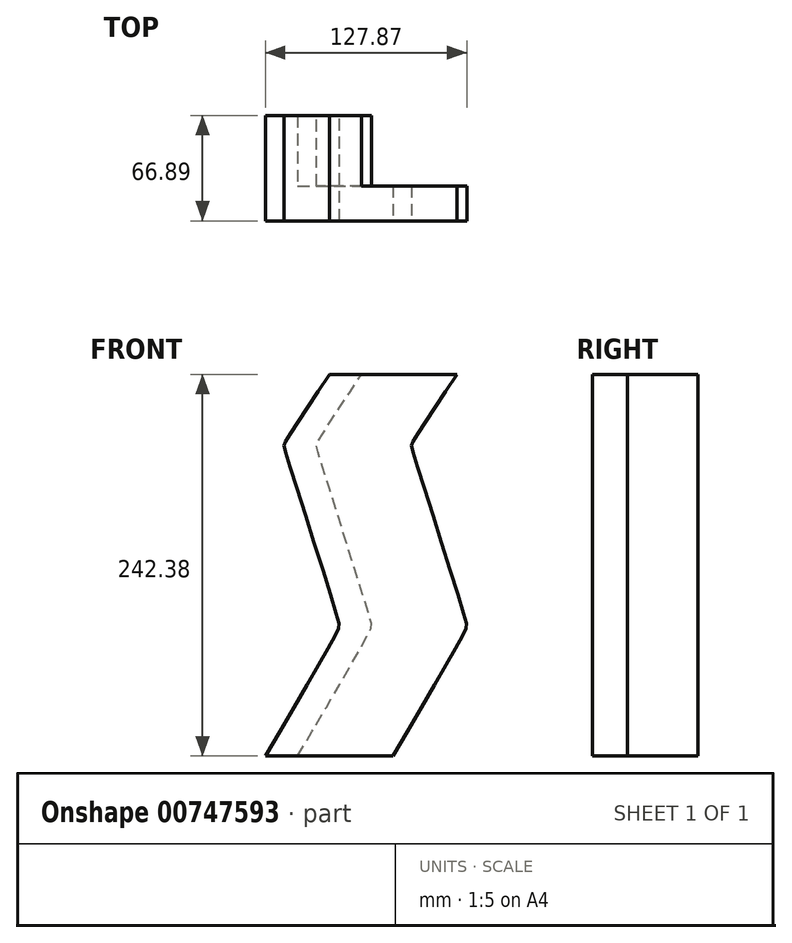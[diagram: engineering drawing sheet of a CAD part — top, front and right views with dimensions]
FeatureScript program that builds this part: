
annotation { "Feature Type Name" : "Feature", "Feature Type Description" : "" }
export const myFeature = defineFeature(function(context is Context, id is Id, definition is map)
    precondition{}
    {
        {
            var Q0;
            Q0=qCreatedBy(makeId("Top.planeOp"),FACE);
            var sketch = newSketch(context, id + "F0", { "sketchPlane" : qUnion([Q0])});
            skLineSegment(sketch, "E0.bottom", {"start": v(-49.6, 34.43) * mm, "end": v(-29.1, 34.43) * mm});
            skLineSegment(sketch, "E0.top", {"start": v(-49.6, -32.46) * mm, "end": v(-29.1, -32.46) * mm});
            skLineSegment(sketch, "E0.left", {"start": v(-49.6, 34.43) * mm, "end": v(-49.6, -32.46) * mm});
            skLineSegment(sketch, "E0.right", {"start": v(-29.1, 34.43) * mm, "end": v(-29.1, -10.26) * mm});
            skLineSegment(sketch, "E1.bottom", {"start": v(-29.1, -10.26) * mm, "end": v(31.34, -10.26) * mm});
            skLineSegment(sketch, "E1.top", {"start": v(-29.1, -32.46) * mm, "end": v(31.34, -32.46) * mm});
            skLineSegment(sketch, "E1.right", {"start": v(31.34, -10.26) * mm, "end": v(31.34, -32.46) * mm});
            skSolve(sketch);
        }
        {
            var Q0;
            Q0=qCreatedBy(makeId("Front.planeOp"),FACE);
            var sketch = newSketch(context, id + "F1", { "sketchPlane" : qUnion([Q0])});
            skFitSpline(sketch, "E2", {"points": [v(-24.89, -105.93) * mm, v(21.04, -26.22) * mm, v(21.04, -18.52) * mm, v(-12.44, 88.45) * mm, v(-12.44, 93.19) * mm, v(15.7, 136.45) * mm], "startDerivative": vector(208.8, 356.04) * mm, "endDerivative": vector(170.38, 257.1) * mm});
            skSolve(sketch);
        }
        {
            var Q0;
            Q0=makeQuery(id+"F0.imprint","IMPRINT",FACE,{"disambiguationData":[TD([[makeQuery(id+"F0.imprint","IMPRINT",EDGE,{"derivedFrom":sQuery(id+"F0.wireOp",EDGE,"E0.bottom")}),-1.0]])]});
            var Q1;
            Q1=sQuery(id+"F1.wireOp",EDGE,"E2");
            sweep(context, id + "F2", {"profiles" : qUnion([Q0]), "path" : qUnion([Q1]), "keepProfileOrientation" : true});
        }
    });
